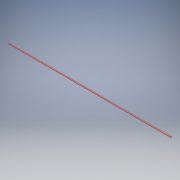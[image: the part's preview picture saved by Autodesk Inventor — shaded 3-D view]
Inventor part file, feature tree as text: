
AUTODESK INVENTOR PART (.ipt)
format: ipt  version: 2016 (Build 200138000, 138)  size: 103,424 bytes
history: native  units: mm
features: extrude x1, sketch x1
ambient origin geometry x8: Origin, YZ Plane, XZ Plane, XY Plane, X Axis, Y Axis, Z Axis, Center Point
bodies: Solid1 (feature_tree)
feature tree (2):
  extrude  "Extrusion1"  Depth=270.0mm TaperAngle=0.0deg
  sketch  "Sketch2"  dims[d0=3.0mm d1=270.0mm d2=0.0mm]
